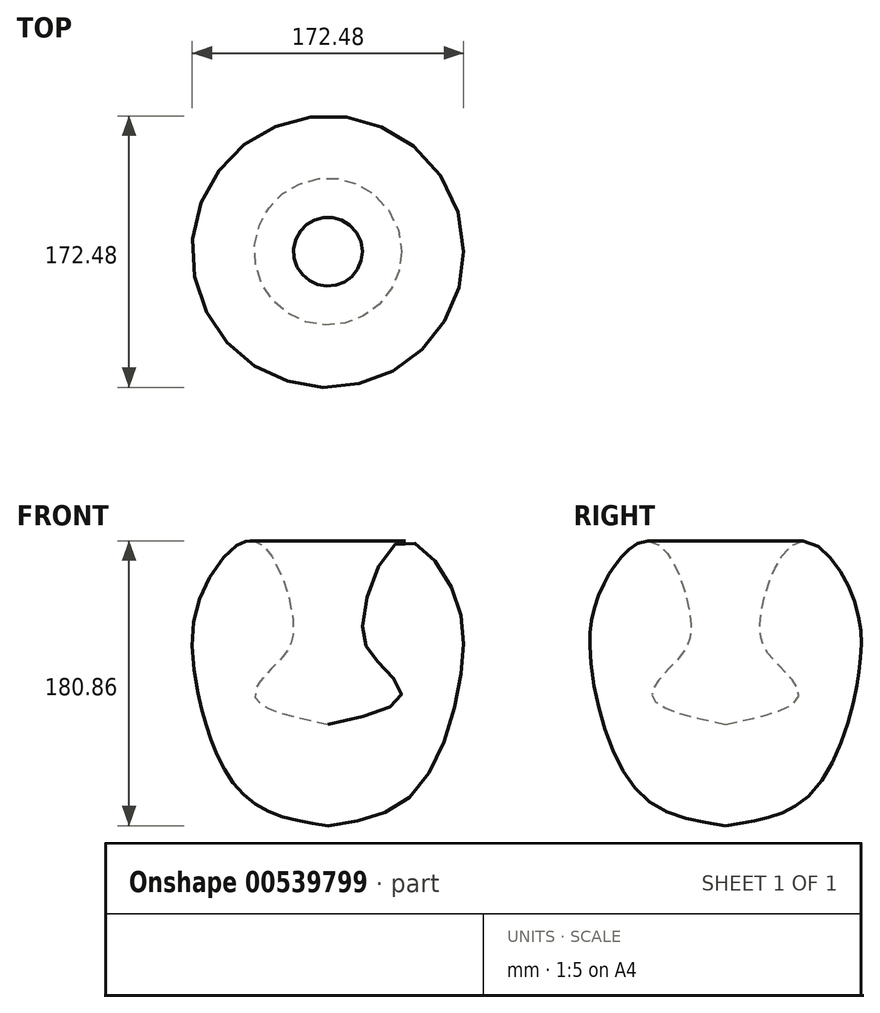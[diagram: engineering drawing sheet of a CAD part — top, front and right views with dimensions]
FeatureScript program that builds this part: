
annotation { "Feature Type Name" : "Feature", "Feature Type Description" : "" }
export const myFeature = defineFeature(function(context is Context, id is Id, definition is map)
    precondition{}
    {
        {
            var Q0;
            Q0=qCreatedBy(makeId("Front.planeOp"),FACE);
            var sketch = newSketch(context, id + "F0", { "sketchPlane" : qUnion([Q0])});
            skFitSpline(sketch, "E0", {"points": [v(0, 0) * mm, v(46.62, 18.15) * mm, v(30.6, 40.8) * mm, v(22.03, 65.67) * mm, v(46.44, 116.07) * mm, v(79.04, 85.5) * mm, v(83.9, 27.23) * mm, v(53.21, -45.13) * mm, v(0, -64.39) * mm], "startDerivative": vector(531.9, 111.12) * mm, "endDerivative": vector(-432.44, -62.78) * mm});
            skLineSegment(sketch, "E1", {"start": v(0, 0) * mm, "end": v(0, -64.39) * mm});
            skSolve(sketch);
        }
        {
            var Q0;
            Q0=makeQuery(id+"F0.imprint","IMPRINT",FACE,{"disambiguationData":[TD([[makeQuery(id+"F0.imprint","IMPRINT",EDGE,{"derivedFrom":sQuery(id+"F0.wireOp",EDGE,"E0")}),-1.0]])]});
            var Q1;
            Q1=sQuery(id+"F0.wireOp",EDGE,"E1");
            revolve(context, id + "F1", {"entities" : qUnion([Q0]), "axis" : qUnion([Q1]), "revolveType" : RevolveType.FULL});
        }
    });
